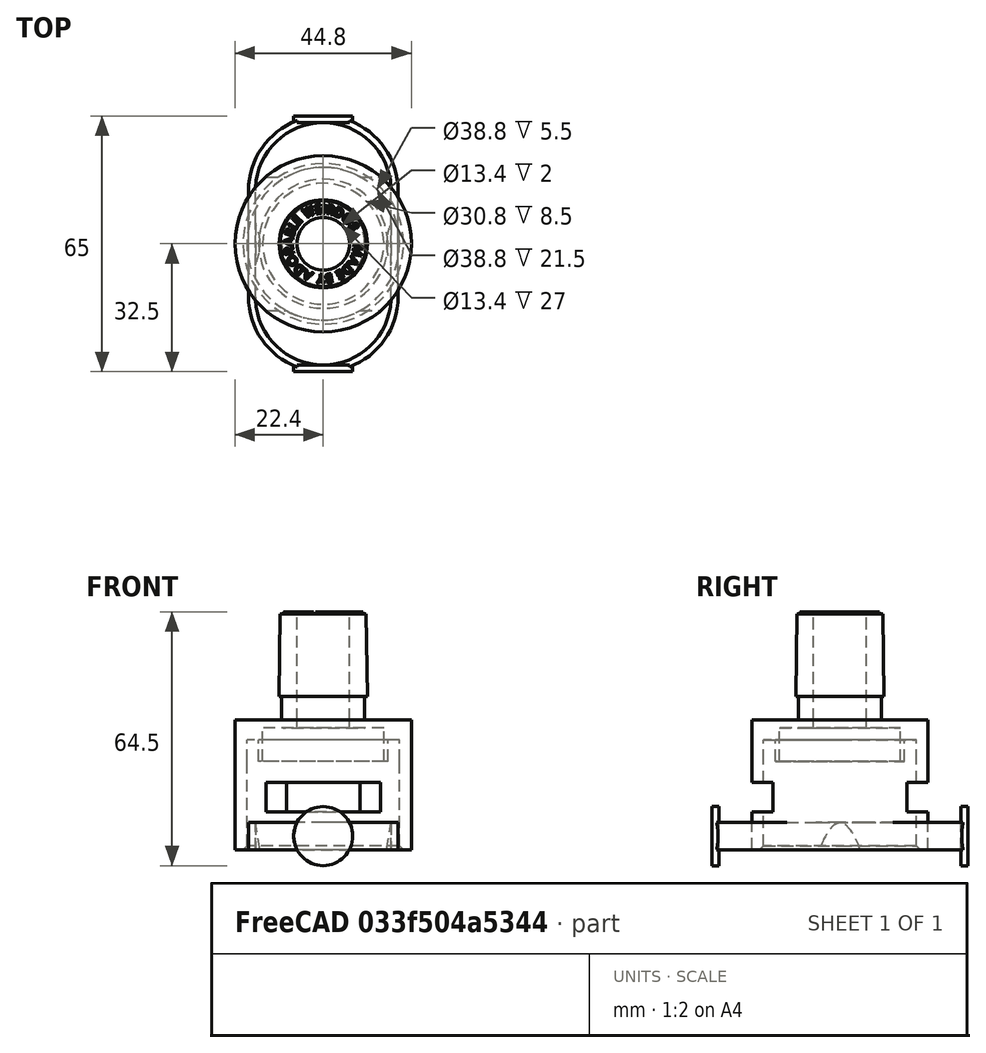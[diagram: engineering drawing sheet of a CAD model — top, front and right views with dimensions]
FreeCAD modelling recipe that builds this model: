
FCSTD DOCUMENT  (FreeCAD 0.18R4 (GitTag))
Label: PAPR-M200-HelmetAdapter
License: All rights reserved
LicenseURL: http://en.wikipedia.org/wiki/All_rights_reserved
objects: Part::Feature×35, Part::Extrusion×35, Part::Cylinder×17, Part::MultiFuse×11, Part::Box×7, Part::Cut×6, Part::Mirroring×3, Part::FeaturePython×2, Part::Cone×1, Part::Chamfer×1
note: 118 computed .brp shape members not serialized (recipe doc carries the construction recipe); baked Part::Feature solids carry a one-line shape summary decoded from their .brp

FEATURE [Part::Cylinder] Cylinder  label="nHelmetAdapterCylinder"
  Angle = 360
  AttacherType = Attacher::AttachEngine3D
  Height = 22.5
  Radius = 19.4
FEATURE [Part::Cylinder] Cylinder001  label="n-pHelmetAdapterGroove"
  Angle = 360
  AttacherType = Attacher::AttachEngine3D
  Height = 28
  Radius = 19.4
FEATURE [Part::Cylinder] Cylinder002  label="n-nHelmetAdapterGroove"
  Angle = 360
  AttacherType = Attacher::AttachEngine3D
  Height = 28
  Radius = 16.4
FEATURE [Part::Cone] Cone001  label="22mmTaper"
  Angle = 360
  AttacherType = Attacher::AttachEngine3D
  Height = 21
  Placement = pos=(0,0,19) rot=(0,0,1;0rad)
  Radius1 = 11.19
  Radius2 = 10.92
FEATURE [Part::Feature] Face029
  shape: bbox 9.744 x 10.08 x 2e-07 mm, 1 faces, 0 solids (baked)
FEATURE [Part::Feature] Face030
  shape: bbox 8.53 x 8.577 x 2e-07 mm, 1 faces, 0 solids (baked)
FEATURE [Part::Feature] Face031
  shape: bbox 2.417 x 1.669 x 2e-07 mm, 1 faces, 0 solids (baked)
FEATURE [Part::Feature] Face032
  shape: bbox 8.554 x 8.603 x 2e-07 mm, 1 faces, 0 solids (baked)
FEATURE [Part::Feature] Face033
  shape: bbox 1.664 x 7.858 x 2e-07 mm, 1 faces, 0 solids (baked)
FEATURE [Part::Feature] Face034
  shape: bbox 2.379 x 2.512 x 2e-07 mm, 1 faces, 0 solids (baked)
FEATURE [Part::Feature] Face035
  shape: bbox 5.568 x 5.6 x 2e-07 mm, 1 faces, 0 solids (baked)
FEATURE [Part::Extrusion] Extrude050
  Base = -> Face032
  Dir = (0,0,1)
  DirMode = 2
  FaceMakerClass = Part::FaceMakerBullseye
  LengthFwd = 0.5
  LengthRev = 0
  Solid = false
  Symmetric = false
FEATURE [Part::Extrusion] Extrude049
  Base = -> Face030
  Dir = (0,0,1)
  DirMode = 2
  FaceMakerClass = Part::FaceMakerBullseye
  LengthFwd = 0.5
  LengthRev = 0
  Solid = false
  Symmetric = false
FEATURE [Part::Extrusion] Extrude053  label="nExtrude027"
  Base = -> Face034
  Dir = (0,0,-1)
  DirMode = 2
  FaceMakerClass = Part::FaceMakerBullseye
  LengthFwd = 0.5
  LengthRev = 0
  Solid = false
  Symmetric = false
FEATURE [Part::Feature] Face059
  shape: bbox 2.64 x 2.607 x 2e-07 mm, 1 faces, 0 solids (baked)
FEATURE [Part::Feature] Face060
  shape: bbox 7.999 x 6.686 x 2e-07 mm, 1 faces, 0 solids (baked)
FEATURE [Part::Feature] Face061
  shape: bbox 7.462 x 8.878 x 2e-07 mm, 1 faces, 0 solids (baked)
FEATURE [Part::Feature] Face040
  shape: bbox 8.613 x 8.371 x 2e-07 mm, 1 faces, 0 solids (baked)
FEATURE [Part::Feature] Face050
  shape: bbox 6.14 x 8.179 x 2e-07 mm, 1 faces, 0 solids (baked)
FEATURE [Part::Extrusion] Extrude047
  Base = -> Face050
  Dir = (0,0,1)
  DirMode = 2
  FaceMakerClass = Part::FaceMakerBullseye
  LengthFwd = 0.5
  LengthRev = 0
  Solid = false
  Symmetric = false
FEATURE [Part::Feature] Face036
  shape: bbox 5.582 x 5.568 x 2e-07 mm, 1 faces, 0 solids (baked)
FEATURE [Part::Feature] Face052
  shape: bbox 8.682 x 5.276 x 2e-07 mm, 1 faces, 0 solids (baked)
FEATURE [Part::Feature] Face038
  shape: bbox 1.801 x 2.496 x 2e-07 mm, 1 faces, 0 solids (baked)
FEATURE [Part::Extrusion] Extrude052  label="nExtrude022"
  Base = -> Face038
  Dir = (0,0,-1)
  DirMode = 2
  FaceMakerClass = Part::FaceMakerBullseye
  LengthFwd = 0.5
  LengthRev = 0
  Solid = false
  Symmetric = false
FEATURE [Part::Feature] Face049
  shape: bbox 8.075 x 7.669 x 2e-07 mm, 1 faces, 0 solids (baked)
FEATURE [Part::Feature] Face043
  shape: bbox 6.283 x 8.728 x 2e-07 mm, 1 faces, 0 solids (baked)
FEATURE [Part::Feature] Face045
  shape: bbox 2.651 x 2.627 x 2e-07 mm, 1 faces, 0 solids (baked)
FEATURE [Part::Extrusion] Extrude051  label="nExtrude001"
  Base = -> Face045
  Dir = (0,0,-1)
  DirMode = 2
  FaceMakerClass = Part::FaceMakerBullseye
  LengthFwd = 0.5
  LengthRev = 0
  Solid = false
  Symmetric = false
FEATURE [Part::Feature] Face053
  shape: bbox 8.573 x 8.602 x 2e-07 mm, 1 faces, 0 solids (baked)
FEATURE [Part::Feature] Face042
  shape: bbox 5.216 x 8.315 x 2e-07 mm, 1 faces, 0 solids (baked)
FEATURE [Part::Feature] Face048
  shape: bbox 1.885 x 1.992 x 2e-07 mm, 1 faces, 0 solids (baked)
FEATURE [Part::Feature] Face044
  shape: bbox 7.415 x 8.972 x 2e-07 mm, 1 faces, 0 solids (baked)
FEATURE [Part::Feature] Face054
  shape: bbox 1.906 x 1.772 x 2e-07 mm, 1 faces, 0 solids (baked)
FEATURE [Part::Feature] Face046
  shape: bbox 2.409 x 2.217 x 2e-07 mm, 1 faces, 0 solids (baked)
FEATURE [Part::Feature] Face055
  shape: bbox 9.184 x 9.463 x 2e-07 mm, 1 faces, 0 solids (baked)
FEATURE [Part::Extrusion] Extrude054
  Base = -> Face055
  Dir = (0,0,1)
  DirMode = 2
  FaceMakerClass = Part::FaceMakerBullseye
  LengthFwd = 0.5
  LengthRev = 0
  Solid = false
  Symmetric = false
FEATURE [Part::Feature] Face056
  shape: bbox 4.509 x 5.218 x 2e-07 mm, 1 faces, 0 solids (baked)
FEATURE [Part::Feature] Face047
  shape: bbox 4.986 x 5.066 x 2e-07 mm, 1 faces, 0 solids (baked)
FEATURE [Part::Feature] Face037
  shape: bbox 4.984 x 5.061 x 2e-07 mm, 1 faces, 0 solids (baked)
FEATURE [Part::Feature] Face051
  shape: bbox 8.497 x 8.592 x 2e-07 mm, 1 faces, 0 solids (baked)
FEATURE [Part::Feature] Face039
  shape: bbox 8.316 x 6.798 x 2e-07 mm, 1 faces, 0 solids (baked)
FEATURE [Part::Feature] Face057
  shape: bbox 6.579 x 8.066 x 2e-07 mm, 1 faces, 0 solids (baked)
FEATURE [Part::Feature] Face041
  shape: bbox 7.94 x 8.569 x 2e-07 mm, 1 faces, 0 solids (baked)
FEATURE [Part::Extrusion] Extrude048
  Base = -> Face041
  Dir = (0,0,1)
  DirMode = 2
  FaceMakerClass = Part::FaceMakerBullseye
  LengthFwd = 0.5
  LengthRev = 0
  Solid = false
  Symmetric = false
FEATURE [Part::Feature] Face058
  shape: bbox 8.512 x 6.398 x 2e-07 mm, 1 faces, 0 solids (baked)
FEATURE [Part::Feature] Face062
  shape: bbox 8.985 x 7.716 x 2e-07 mm, 1 faces, 0 solids (baked)
FEATURE [Part::Feature] Face063
  shape: bbox 2.472 x 1.907 x 2e-07 mm, 1 faces, 0 solids (baked)
FEATURE [Part::Extrusion] Extrude064  label="nExtrude015"
  Base = -> Face056
  Dir = (0,0,-1)
  DirMode = 2
  FaceMakerClass = Part::FaceMakerBullseye
  LengthFwd = 0.5
  LengthRev = 0
  Solid = false
  Symmetric = false
FEATURE [Part::Extrusion] Extrude062  label="nExtrude010"
  Base = -> Face035
  Dir = (0,0,-1)
  DirMode = 2
  FaceMakerClass = Part::FaceMakerBullseye
  LengthFwd = 0.5
  LengthRev = 0
  Solid = false
  Symmetric = false
FEATURE [Part::Extrusion] Extrude065  label="nExtrude006"
  Base = -> Face036
  Dir = (0,0,-1)
  DirMode = 2
  FaceMakerClass = Part::FaceMakerBullseye
  LengthFwd = 0.5
  LengthRev = 0
  Solid = false
  Symmetric = false
FEATURE [Part::Extrusion] Extrude061  label="nExtrude003"
  Base = -> Face046
  Dir = (0,0,-1)
  DirMode = 2
  FaceMakerClass = Part::FaceMakerBullseye
  LengthFwd = 0.5
  LengthRev = 0
  Solid = false
  Symmetric = false
FEATURE [Part::Extrusion] Extrude066  label="nExtrude012"
  Base = -> Face047
  Dir = (0,0,-1)
  DirMode = 2
  FaceMakerClass = Part::FaceMakerBullseye
  LengthFwd = 0.5
  LengthRev = 0
  Solid = false
  Symmetric = false
FEATURE [Part::Extrusion] Extrude067
  Base = -> Face052
  Dir = (0,0,1)
  DirMode = 2
  FaceMakerClass = Part::FaceMakerBullseye
  LengthFwd = 0.5
  LengthRev = 0
  Solid = false
  Symmetric = false
FEATURE [Part::Extrusion] Extrude059  label="nExtrude014"
  Base = -> Face037
  Dir = (0,0,-1)
  DirMode = 2
  FaceMakerClass = Part::FaceMakerBullseye
  LengthFwd = 0.5
  LengthRev = 0
  Solid = false
  Symmetric = false
FEATURE [Part::Extrusion] Extrude055
  Base = -> Face040
  Dir = (0,0,1)
  DirMode = 2
  FaceMakerClass = Part::FaceMakerBullseye
  LengthFwd = 0.5
  LengthRev = 0
  Solid = false
  Symmetric = false
FEATURE [Part::Extrusion] Extrude063
  Base = -> Face033
  Dir = (0,0,1)
  DirMode = 2
  FaceMakerClass = Part::FaceMakerBullseye
  LengthFwd = 0.5
  LengthRev = 0
  Solid = false
  Symmetric = false
FEATURE [Part::Extrusion] Extrude056
  Base = -> Face029
  Dir = (0,0,1)
  DirMode = 2
  FaceMakerClass = Part::FaceMakerBullseye
  LengthFwd = 0.5
  LengthRev = 0
  Solid = false
  Symmetric = false
FEATURE [Part::Extrusion] Extrude057
  Base = -> Face051
  Dir = (0,0,1)
  DirMode = 2
  FaceMakerClass = Part::FaceMakerBullseye
  LengthFwd = 0.5
  LengthRev = 0
  Solid = false
  Symmetric = false
FEATURE [Part::Extrusion] Extrude058  label="nExtrude013"
  Base = -> Face048
  Dir = (0,0,-1)
  DirMode = 2
  FaceMakerClass = Part::FaceMakerBullseye
  LengthFwd = 0.5
  LengthRev = 0
  Solid = false
  Symmetric = false
FEATURE [Part::Extrusion] Extrude060
  Base = -> Face044
  Dir = (0,0,1)
  DirMode = 2
  FaceMakerClass = Part::FaceMakerBullseye
  LengthFwd = 0.5
  LengthRev = 0
  Solid = false
  Symmetric = false
FEATURE [Part::Extrusion] Extrude075
  Base = -> Face060
  Dir = (0,0,1)
  DirMode = 2
  FaceMakerClass = Part::FaceMakerBullseye
  LengthFwd = 0.5
  LengthRev = 0
  Solid = false
  Symmetric = false
FEATURE [Part::Extrusion] Extrude073  label="nExtrude025"
  Base = -> Face031
  Dir = (0,0,-1)
  DirMode = 2
  FaceMakerClass = Part::FaceMakerBullseye
  LengthFwd = 0.5
  LengthRev = 0
  Solid = false
  Symmetric = false
FEATURE [Part::Extrusion] Extrude029
  Base = -> Face043
  Dir = (0,0,1)
  DirMode = 2
  FaceMakerClass = Part::FaceMakerBullseye
  LengthFwd = 0.5
  LengthRev = 0
  Solid = false
  Symmetric = false
FEATURE [Part::Extrusion] Extrude069
  Base = -> Face057
  Dir = (0,0,1)
  DirMode = 2
  FaceMakerClass = Part::FaceMakerBullseye
  LengthFwd = 0.5
  LengthRev = 0
  Solid = false
  Symmetric = false
FEATURE [Part::Extrusion] Extrude068
  Base = -> Face049
  Dir = (0,0,1)
  DirMode = 2
  FaceMakerClass = Part::FaceMakerBullseye
  LengthFwd = 0.5
  LengthRev = 0
  Solid = false
  Symmetric = false
FEATURE [Part::Extrusion] Extrude071
  Base = -> Face042
  Dir = (0,0,1)
  DirMode = 2
  FaceMakerClass = Part::FaceMakerBullseye
  LengthFwd = 0.5
  LengthRev = 0
  Solid = false
  Symmetric = false
FEATURE [Part::Extrusion] Extrude077
  Base = -> Face062
  Dir = (0,0,1)
  DirMode = 2
  FaceMakerClass = Part::FaceMakerBullseye
  LengthFwd = 0.5
  LengthRev = 0
  Solid = false
  Symmetric = false
FEATURE [Part::Extrusion] Extrude078  label="nExtrude032"
  Base = -> Face063
  Dir = (0,0,-1)
  DirMode = 2
  FaceMakerClass = Part::FaceMakerBullseye
  LengthFwd = 0.5
  LengthRev = 0
  Solid = false
  Symmetric = false
FEATURE [Part::Extrusion] Extrude030  label="nExtrude030"
  Base = -> Face059
  Dir = (0,0,-1)
  DirMode = 2
  FaceMakerClass = Part::FaceMakerBullseye
  LengthFwd = 0.5
  LengthRev = 0
  Solid = false
  Symmetric = false
FEATURE [Part::Extrusion] Extrude072  label="nExtrude024"
  Base = -> Face054
  Dir = (0,0,-1)
  DirMode = 2
  FaceMakerClass = Part::FaceMakerBullseye
  LengthFwd = 0.5
  LengthRev = 0
  Solid = false
  Symmetric = false
FEATURE [Part::MultiFuse] Fusion070  label="nExtrude"
  Shapes = -> [Extrude078,Extrude030,Extrude053,Extrude073,Extrude072,Extrude052,Extrude064,Extrude059,Extrude058,Extrude066,Extrude062,Extrude065,Extrude051,Extrude061]
FEATURE [Part::Mirroring] Part__Mirroring009  label="nMadeByAdorableWeirdos"
  Base = (0,0,0)
  Normal = (0,0,1)
  Source = -> Fusion070
FEATURE [Part::Extrusion] Extrude074
  Base = -> Face039
  Dir = (0,0,1)
  DirMode = 2
  FaceMakerClass = Part::FaceMakerBullseye
  LengthFwd = 0.5
  LengthRev = 0
  Solid = false
  Symmetric = false
FEATURE [Part::Extrusion] Extrude076
  Base = -> Face061
  Dir = (0,0,1)
  DirMode = 2
  FaceMakerClass = Part::FaceMakerBullseye
  LengthFwd = 0.5
  LengthRev = 0
  Solid = false
  Symmetric = false
FEATURE [Part::Extrusion] Extrude070
  Base = -> Face053
  Dir = (0,0,1)
  DirMode = 2
  FaceMakerClass = Part::FaceMakerBullseye
  LengthFwd = 0.5
  LengthRev = 0
  Solid = false
  Symmetric = false
FEATURE [Part::Extrusion] Extrude079
  Base = -> Face058
  Dir = (0,0,1)
  DirMode = 2
  FaceMakerClass = Part::FaceMakerBullseye
  LengthFwd = 0.5
  LengthRev = 0
  Solid = false
  Symmetric = false
FEATURE [Part::MultiFuse] Fusion071  label="pMadeByAdorableWeirdos"
  Shapes = -> [Extrude054,Extrude047,Extrude048,Extrude049,Extrude050,Extrude055,Extrude056,Extrude057,Extrude060,Extrude063,Extrude067,Extrude068,Extrude069,Extrude070,Extrude071,Extrude074,Extrude029,Extrude075,Extrude076,Extrude077,Extrude079]
FEATURE [Part::Cut] Cut031  label="MadeByAdorableWeirdos"
  Base = -> Fusion071
  Tool = -> Part__Mirroring009
FEATURE [Part::FeaturePython] Clone001  label="MadeByAdorableWeirdos-ScaledClone"  # Draft clone (typed FeaturePython)
  AttacherType = Attacher::AttachEngine3D
  Fuse = false
  Objects = -> [Cut031]
  Placement = pos=(-29.85,42.85,40) rot=(1,0,0;0rad)
  Scale = (0.3,0.3,1)
FEATURE [Part::Cylinder] Cylinder005  label="nOutletTube"
  Angle = 360
  AttacherType = Attacher::AttachEngine3D
  Height = 40
  Radius = 6.7
FEATURE [Part::Cylinder] Cylinder019  label="HousingOutlet"
  Angle = 360
  AttacherType = Attacher::AttachEngine3D
  Height = 40
  Radius = 10.55
FEATURE [Part::MultiFuse] Fusion072  label="pOutletExtension"
  Shapes = -> [Clone001,Cone001,Cylinder019]
FEATURE [Part::Cut] Cut033  label="nHelmetAdapterGroove"
  Base = -> Cylinder001
  Tool = -> Cylinder002
FEATURE [Part::Cylinder] Cylinder064  label="nHelmetAdapterPipe"
  Angle = 360
  AttacherType = Attacher::AttachEngine3D
  Height = 31
  Radius = 15.4
FEATURE [Part::Cylinder] Cylinder065  label="pHelmetAdapterBody"
  Angle = 360
  AttacherType = Attacher::AttachEngine3D
  Height = 33
  Radius = 22.4
FEATURE [Part::MultiFuse] Fusion073  label="nHelmetAdapterBase"
  Shapes = -> [Cylinder064,Cut033,Cylinder]
FEATURE [Part::Cut] Cut  label="HoseAdapter"
  Base = -> Fusion072
  Placement = pos=(0,0,20) rot=(0,0,1;0rad)
  Tool = -> Cylinder005
FEATURE [Part::Box] Box  label="nAttachNotch1"
  AttacherType = Attacher::AttachEngine3D
  Height = 7.5
  Length = 29.5
  Placement = pos=(-14.75,17,9.6) rot=(0,0,1;0rad)
  Width = 10
FEATURE [Part::Box] Box001  label="nAttachNotch2"
  AttacherType = Attacher::AttachEngine3D
  Height = 7.5
  Length = 29.5
  Placement = pos=(-14.75,-27,9.6) rot=(0,0,1;0rad)
  Width = 10
FEATURE [Part::MultiFuse] Fusion  label="nHelmetAdapter"
  Shapes = -> [Fusion073,Box001,Box]
FEATURE [Part::Cut] Cut034  label="HelmetAdapterBodyMinusChamfer"
  Base = -> Cylinder065
  Tool = -> Fusion
FEATURE [Part::Chamfer] Chamfer  label="HelmetAdapterBody"
  Base = -> Cut034
  Edges = 1 edges r=1: [Edge12]
FEATURE [Part::FeaturePython] Connect  label="TopLevelPart-HelmetAdapter"  # WARN: FeaturePython — macro-defined, semantics opaque (R4)
  Objects = -> [Chamfer,Cut]
  Tolerance = 0
FEATURE [Part::Cylinder] Cylinder066  label="pLockCylinderUpper"
  Angle = 360
  AttacherType = Attacher::AttachEngine3D
  Height = 7
  Placement = pos=(0,13.5,0) rot=(0,0,1;0rad)
  Radius = 19
FEATURE [Part::Cylinder] Cylinder067  label="nLockCylinderUpper"
  Angle = 360
  AttacherType = Attacher::AttachEngine3D
  Height = 7
  Placement = pos=(0,13.5,0) rot=(0,0,1;0rad)
  Radius = 17.25
FEATURE [Part::Box] Box002  label="pLockRingStraight1"
  AttacherType = Attacher::AttachEngine3D
  Height = 7
  Length = 1.75
  Placement = pos=(17.25,-13.5,0) rot=(0,0,1;0rad)
  Width = 27
FEATURE [Part::Box] Box003  label="pLockRingStraight2"
  AttacherType = Attacher::AttachEngine3D
  Height = 7
  Length = 1.75
  Placement = pos=(-19,-13.5,0) rot=(0,0,1;0rad)
  Width = 27
FEATURE [Part::Box] Box004  label="Cube002"
  AttacherType = Attacher::AttachEngine3D
  Height = 7
  Length = 40
  Placement = pos=(19,-13.5,0) rot=(0,0,1;0rad)
  Width = 27
FEATURE [Part::Box] Box005  label="Cube003"
  AttacherType = Attacher::AttachEngine3D
  Height = 7
  Length = 40
  Placement = pos=(-59,-13.5,0) rot=(0,0,1;0rad)
  Width = 27
FEATURE [Part::MultiFuse] Fusion075  label="nFlats"
  Shapes = -> [Box004,Box005]
FEATURE [Part::Cylinder] Cylinder069  label="nCylinder001"
  Angle = 360
  AttacherType = Attacher::AttachEngine3D
  Height = 10
  Placement = pos=(0,0,7) rot=(0,0,1;0rad)
  Radius = 80
FEATURE [Part::Cylinder] Cylinder070  label="nCylinder002"
  Angle = 360
  AttacherType = Attacher::AttachEngine3D
  Height = 10
  Placement = pos=(0,0,-10) rot=(0,0,1;0rad)
  Radius = 80
FEATURE [Part::Cylinder] Cylinder071  label="pLockRingTooth"
  Angle = 360
  AttacherType = Attacher::AttachEngine3D
  Height = 10
  Placement = pos=(-27.5462,0,-3.88689) rot=(0,1,0;6.10865rad)
  Radius = 12
FEATURE [Part::MultiFuse] Fusion077  label="nLockRing"
  Shapes = -> [Fusion075,Cylinder070,Cylinder069]
FEATURE [Part::Cylinder] Cylinder072  label="pLockCylinderLower"
  Angle = 360
  AttacherType = Attacher::AttachEngine3D
  Height = 7
  Placement = pos=(0,-13.5,0) rot=(0,0,1;0rad)
  Radius = 19
FEATURE [Part::Cylinder] Cylinder073  label="nLockCylinderLower"
  Angle = 360
  AttacherType = Attacher::AttachEngine3D
  Height = 7
  Placement = pos=(0,-13.5,0) rot=(0,0,1;0rad)
  Radius = 17.25
FEATURE [Part::Box] Box006  label="nLockCylinderBlock"
  AttacherType = Attacher::AttachEngine3D
  Height = 7
  Length = 34.5
  Placement = pos=(-17.25,-13.5,0) rot=(0,0,1;0rad)
  Width = 27
FEATURE [Part::MultiFuse] Fusion078  label="nLockCylinder"
  Shapes = -> [Box006,Cylinder073,Cylinder067]
FEATURE [Part::MultiFuse] Fusion079  label="pLockCylinder"
  Shapes = -> [Cylinder066,Cylinder072]
FEATURE [Part::Cut] Cut035  label="pLockRingTrackRounds"
  Base = -> Fusion079
  Tool = -> Fusion078
FEATURE [Part::Mirroring] Part__Mirroring  label="pLockRingTooth2"
  Base = (0,0,0)
  Normal = (1,0,0)
  Source = -> Cylinder071
FEATURE [Part::Cylinder] Cylinder075  label="FingerTab"
  Angle = 360
  AttacherType = Attacher::AttachEngine3D
  Height = 1.75
  Placement = pos=(0,-30.75,3.5) rot=(1,0,0;1.5708rad)
  Radius = 7.5
FEATURE [Part::Mirroring] Part__Mirroring010  label="FingerTab2"
  Base = (0,0,0)
  Normal = (0,1,0)
  Source = -> Cylinder075
FEATURE [Part::Cylinder] Cylinder076  label="pLockRingTooth1"
  Angle = 360
  AttacherType = Attacher::AttachEngine3D
  Height = 10
  Placement = pos=(-27.5462,0,-3.88689) rot=(0,-1,0;0.174533rad)
  Radius = 12
FEATURE [Part::MultiFuse] Fusion080  label="pLockRing"
  Shapes = -> [Cylinder076,Part__Mirroring,Box002,Cut035,Box003]
FEATURE [Part::Cut] Cut036  label="LockRingNoFingerTabs"
  Base = -> Fusion080
  Tool = -> Fusion077
FEATURE [Part::Cylinder] Cylinder077  label="FingerTab1"
  Angle = 360
  AttacherType = Attacher::AttachEngine3D
  Height = 1.75
  Placement = pos=(0,-30.75,3.5) rot=(1,0,0;1.5708rad)
  Radius = 7.5
FEATURE [Part::MultiFuse] Fusion081  label="TopLevelPart-LockRing"
  Shapes = -> [Part__Mirroring010,Cut036,Cylinder077]
